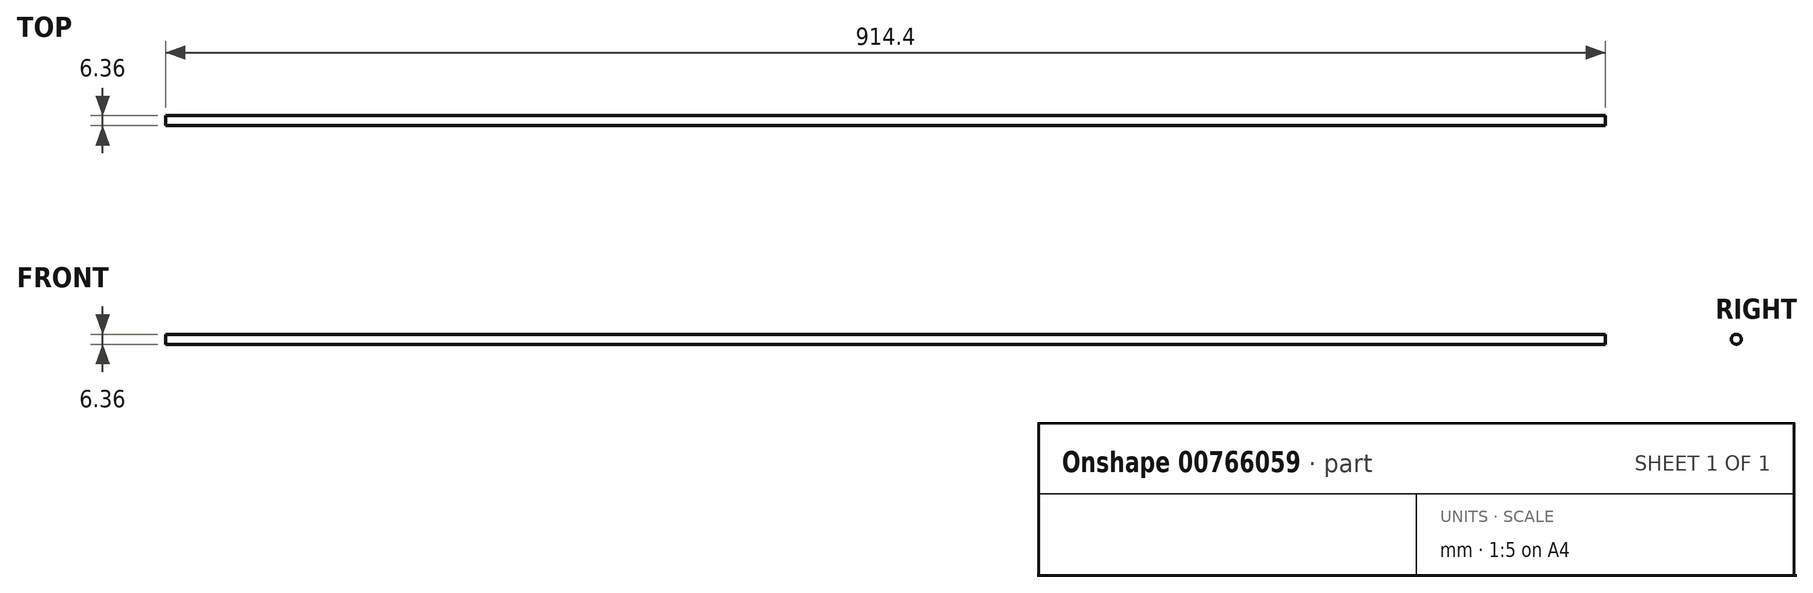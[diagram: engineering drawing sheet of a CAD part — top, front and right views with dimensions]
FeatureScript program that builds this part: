
annotation { "Feature Type Name" : "Feature", "Feature Type Description" : "" }
export const myFeature = defineFeature(function(context is Context, id is Id, definition is map)
    precondition{}
    {
        {
            var Q0;
            Q0=qCreatedBy(makeId("Right.planeOp"),FACE);
            var sketch = newSketch(context, id + "F0", { "sketchPlane" : qUnion([Q0])});
            skCircle(sketch, "E0", {"center": v(0, 0) * mm, "radius": 3.18 * mm});
            skSolve(sketch);
        }
        {
            var Q0;
            Q0=makeQuery(id+"F0.imprint","IMPRINT",FACE,{"disambiguationData":[TD([[makeQuery(id+"F0.imprint","IMPRINT",EDGE,{"derivedFrom":sQuery(id+"F0.wireOp",EDGE,"E0")}),1.0]])]});
            extrude(context, id + "F1", {"entities" : qUnion([Q0]), "depth" : 914.4 * mm, "offsetDistance" : 25.4 * mm});
        }
    });
